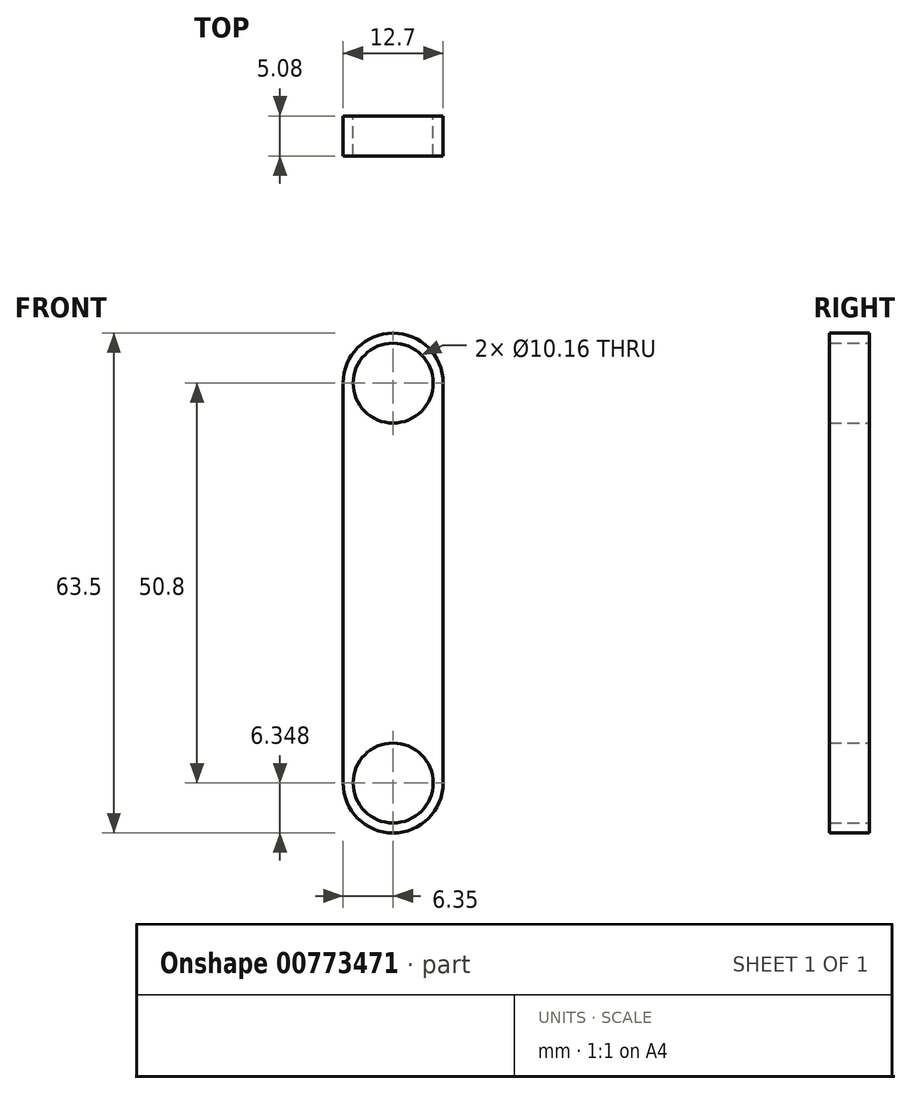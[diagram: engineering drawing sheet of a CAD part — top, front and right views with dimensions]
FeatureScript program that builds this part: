
annotation { "Feature Type Name" : "Feature", "Feature Type Description" : "" }
export const myFeature = defineFeature(function(context is Context, id is Id, definition is map)
    precondition{}
    {
        {
            var Q0;
            Q0=qCreatedBy(makeId("Front.planeOp"),FACE);
            var sketch = newSketch(context, id + "F0", { "sketchPlane" : qUnion([Q0])});
            skCircle(sketch, "E0", {"center": v(0, 19.16) * mm, "radius": 6.35 * mm});
            skCircle(sketch, "E1", {"center": v(0, 19.16) * mm, "radius": 5.08 * mm});
            skCircle(sketch, "E2", {"center": v(0, -31.64) * mm, "radius": 6.35 * mm});
            skCircle(sketch, "E3", {"center": v(0, -31.64) * mm, "radius": 5.08 * mm});
            skLineSegment(sketch, "E4", {"start": v(-6.35, 19.16) * mm, "end": v(-6.35, -31.64) * mm});
            skLineSegment(sketch, "E5", {"start": v(6.35, -31.64) * mm, "end": v(6.35, 19.16) * mm});
            skSolve(sketch);
        }
        {
            var Q0;
            {var subQ0=sQuery(id+"F0.wireOp",EDGE,"E4");Q0=makeQuery(id+"F0.imprint","IMPRINT",FACE,{"disambiguationData":[TD([[makeQuery(id+"F0.imprint","IMPRINT",EDGE,{"derivedFrom":subQ0}),1.0]])]});}
            var Q1;
            Q1=makeQuery(id+"F0.imprint","IMPRINT",FACE,{"disambiguationData":[TD([[makeQuery(id+"F0.imprint","IMPRINT",EDGE,{"derivedFrom":sQuery(id+"F0.wireOp",EDGE,"E1")}),-1.0]])]});
            var Q2;
            Q2=makeQuery(id+"F0.imprint","IMPRINT",FACE,{"disambiguationData":[TD([[makeQuery(id+"F0.imprint","IMPRINT",EDGE,{"derivedFrom":sQuery(id+"F0.wireOp",EDGE,"E3")}),-1.0]])]});
            extrude(context, id + "F1", {"entities" : qUnion([Q0, Q1, Q2]), "depth" : 5.08 * mm, "offsetDistance" : 25.4 * mm});
        }
    });
